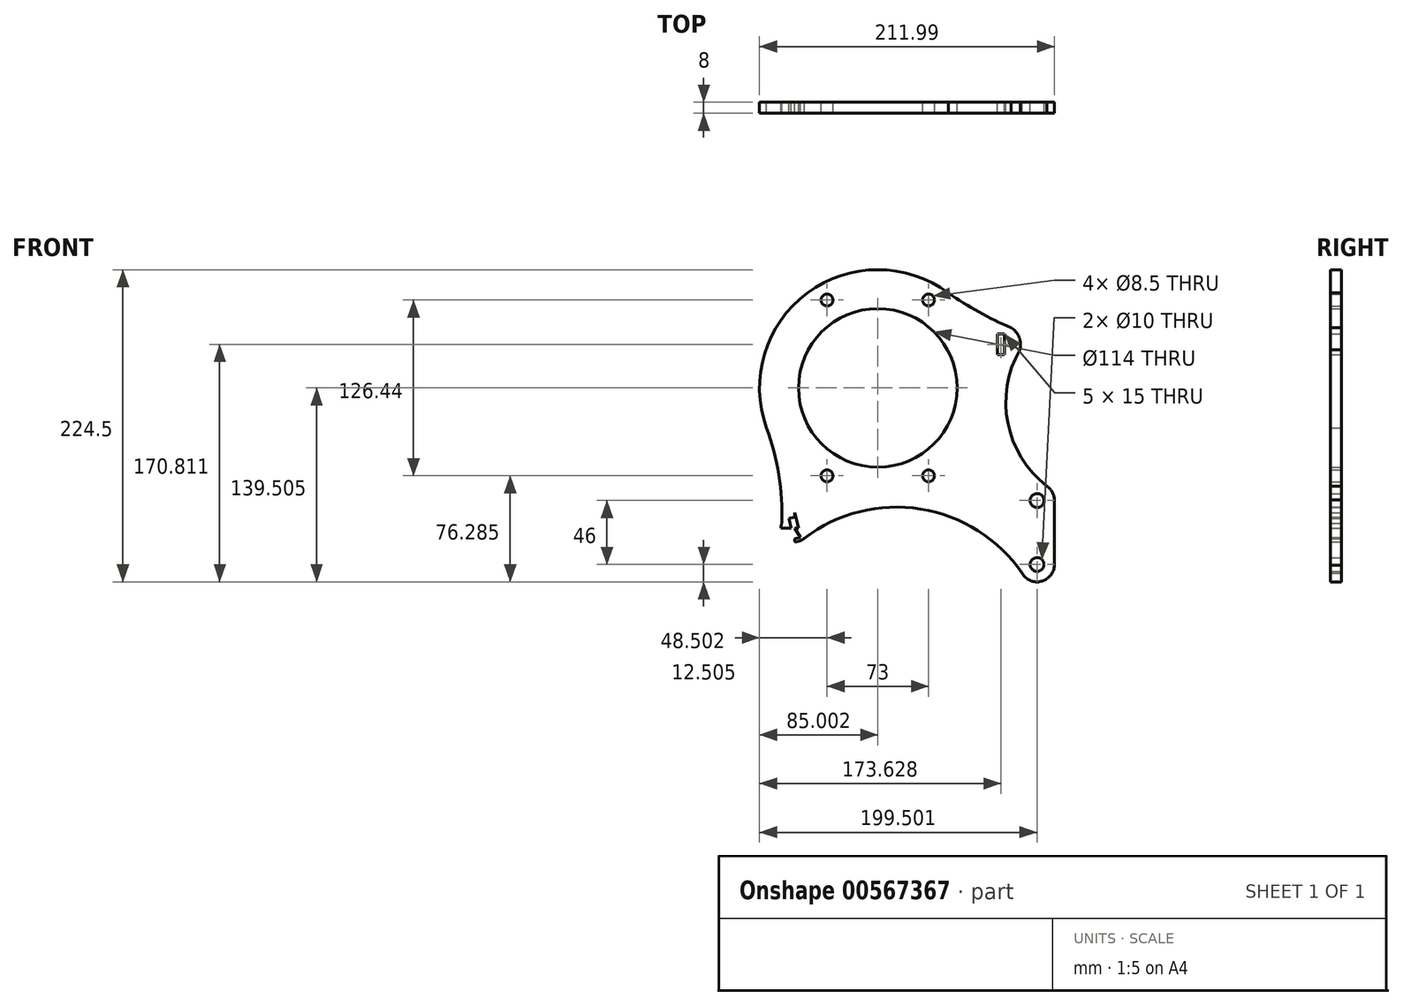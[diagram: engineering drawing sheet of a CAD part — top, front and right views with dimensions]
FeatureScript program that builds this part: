
annotation { "Feature Type Name" : "Feature", "Feature Type Description" : "" }
export const myFeature = defineFeature(function(context is Context, id is Id, definition is map)
    precondition{}
    {
        {
            var Q0;
            Q0=qCreatedBy(makeId("Front.planeOp"),FACE);
            var sketch = newSketch(context, id + "F0", { "sketchPlane" : qUnion([Q0])});
            skLineSegment(sketch, "E0", {"start": v(-75.21, -79.5) * mm, "end": v(137.4, -79.5) * mm});
            skLineSegment(sketch, "E1", {"start": v(96.05, -79.5) * mm, "end": v(96.05, -33.5) * mm});
            skCircle(sketch, "E2", {"center": v(96.05, -79.5) * mm, "radius": 5 * mm});
            skCircle(sketch, "E3", {"center": v(96.05, -33.5) * mm, "radius": 5 * mm});
            skLineSegment(sketch, "E4", {"start": v(72.68, 86.31) * mm, "end": v(72.68, 71.31) * mm});
            skLineSegment(sketch, "E5", {"start": v(72.68, 71.31) * mm, "end": v(67.68, 71.31) * mm});
            skLineSegment(sketch, "E6", {"start": v(67.68, 71.31) * mm, "end": v(67.68, 86.31) * mm});
            skLineSegment(sketch, "E7", {"start": v(22.56, -60.46) * mm, "end": v(-105.66, -60.46) * mm});
            skLineSegment(sketch, "E8", {"start": v(-45.55, -47.65) * mm, "end": v(-86.37, -47.65) * mm});
            skLineSegment(sketch, "E9", {"start": v(-80.4, -31.86) * mm, "end": v(-76.76, -47.65) * mm});
            skArc(sketch, "E10", {"start": v(85.3, -85.88) * mm, "mid": v(99.56, -91.5) * mm, "end": v(108.54, -79.1) * mm});
            skArc(sketch, "E11", {"start": v(108.54, -33.9) * mm, "mid": v(107.16, -27.77) * mm, "end": v(102.97, -23.09) * mm});
            skLineSegment(sketch, "E12", {"start": v(67.68, 86.31) * mm, "end": v(72.68, 71.31) * mm});
            skLineSegment(sketch, "E13", {"start": v(72.68, 86.31) * mm, "end": v(67.68, 71.31) * mm});
            skPoint(sketch, "E14", {"position": v(70.18, 78.81) * mm});
            skLineSegment(sketch, "E15", {"start": v(-80.4, -31.86) * mm, "end": v(-73.67, -61.07) * mm});
            skLineSegment(sketch, "E16", {"start": v(108.54, -33.1) * mm, "end": v(108.54, -79.9) * mm});
            skLineSegment(sketch, "E17", {"start": v(-77.3, -45.33) * mm, "end": v(-82.17, -46.45) * mm});
            skLineSegment(sketch, "E18", {"start": v(-82.17, -46.45) * mm, "end": v(-78.8, -61.07) * mm});
            skLineSegment(sketch, "E19", {"start": v(-78.8, -61.07) * mm, "end": v(-73.92, -59.94) * mm});
            skLineSegment(sketch, "E20", {"start": v(-77.3, -45.33) * mm, "end": v(-78.8, -61.07) * mm});
            skLineSegment(sketch, "E21", {"start": v(-82.17, -46.45) * mm, "end": v(-73.92, -59.94) * mm});
            skPoint(sketch, "E22", {"position": v(-78.05, -53.2) * mm});
            skCircle(sketch, "E23", {"center": v(-78.05, -53.2) * mm, "radius": 10 * mm});
            skLineSegment(sketch, "E24", {"start": v(-2.45, 33.5) * mm, "end": v(-113.64, 33.5) * mm});
            skLineSegment(sketch, "E25", {"start": v(-78.05, -53.2) * mm, "end": v(-78.05, -19.4) * mm});
            skLineSegment(sketch, "E26", {"start": v(-78.05, -47.35) * mm, "end": v(-78.05, -67.2) * mm});
            skLineSegment(sketch, "E27", {"start": v(-89.21, -53.2) * mm, "end": v(-73.06, -53.2) * mm});
            skLineSegment(sketch, "E28", {"start": v(-2.45, 33.5) * mm, "end": v(-2.45, -63.27) * mm});
            skLineSegment(sketch, "E29.trimOffspring", {"start": v(52.9, 86.31) * mm, "end": v(72.68, 86.31) * mm});
            skArc(sketch, "E30", {"start": v(83.65, 74.99) * mm, "mid": v(83.21, 83.92) * mm, "end": v(77.47, 90.76) * mm});
            skPoint(sketch, "E31.end.orphan", {"position": v(-78.95, 33.5) * mm});
            skArc(sketch, "E32", {"start": v(83.65, 74.99) * mm, "mid": v(75.05, 22.35) * mm, "end": v(102.97, -23.09) * mm});
            skArc(sketch, "E33", {"start": v(85.3, -85.88) * mm, "mid": v(12.4, -39.6) * mm, "end": v(-71.35, -60.62) * mm});
            skCircle(sketch, "E34", {"center": v(-18.45, 47.5) * mm, "radius": 57 * mm});
            skCircle(sketch, "E35", {"center": v(-18.45, 47.5) * mm, "radius": 73 * mm});
            skLineSegment(sketch, "E36", {"start": v(-18.45, 47.5) * mm, "end": v(-117.37, 47.5) * mm});
            skLineSegment(sketch, "E37", {"start": v(-18.45, 47.5) * mm, "end": v(-61.37, 121.85) * mm});
            skLineSegment(sketch, "E38", {"start": v(-18.45, 47.5) * mm, "end": v(25.25, 123.2) * mm});
            skLineSegment(sketch, "E39", {"start": v(-18.45, 47.5) * mm, "end": v(28.36, -33.57) * mm});
            skLineSegment(sketch, "E40", {"start": v(-18.45, 47.5) * mm, "end": v(-53.64, -13.44) * mm});
            skCircle(sketch, "E41", {"center": v(-54.95, 110.72) * mm, "radius": 4.25 * mm});
            skCircle(sketch, "E42", {"center": v(18.05, 110.72) * mm, "radius": 4.25 * mm});
            skCircle(sketch, "E43", {"center": v(18.05, -15.72) * mm, "radius": 4.25 * mm});
            skCircle(sketch, "E44", {"center": v(-54.95, -15.72) * mm, "radius": 4.25 * mm});
            skCircle(sketch, "E45", {"center": v(-18.45, 47.5) * mm, "radius": 85 * mm});
            skArc(sketch, "E46", {"start": v(-87.5, -49.93) * mm, "mid": v(-89.52, -15.05) * mm, "end": v(-98.43, 18.74) * mm});
            skArc(sketch, "E47", {"start": v(32.24, 115.74) * mm, "mid": v(54.23, 102.13) * mm, "end": v(77.47, 90.76) * mm});
            skSolve(sketch);
        }
        {
            var Q0;
            {var subQ1=sQuery(id+"F0.wireOp",EDGE,"E8");var subQ5=sQuery(id+"F0.wireOp",EDGE,"E33");var subQ6=makeQuery(id+"F0.imprint","INTERSECT",VERTEX,{"derivedFrom":[subQ1,subQ5]});Q0=makeQuery(id+"F0.imprint","IMPRINT",FACE,{"disambiguationData":[TD([[makeQuery(id+"F0.imprint","IMPRINT",EDGE,{"disambiguationData":[TD([[subQ6,-1.0]])],"derivedFrom":subQ1}),-1.0]])]});}
            var Q1;
            {var subQ0=sQuery(id+"F0.wireOp",EDGE,"E23");var subQ1=sQuery(id+"F0.wireOp",EDGE,"E8");var subQ2=makeQuery(id+"F0.imprint","INTERSECT",VERTEX,{"disambiguationData":[OD(0.0)],"derivedFrom":[subQ1,subQ0]});Q1=makeQuery(id+"F0.imprint","IMPRINT",FACE,{"disambiguationData":[TD([[makeQuery(id+"F0.imprint","IMPRINT",EDGE,{"disambiguationData":[TD([[subQ2,1.0]])],"derivedFrom":subQ1}),1.0]])]});}
            var Q2;
            {var subQ0=sQuery(id+"F0.wireOp",EDGE,"E23");var subQ1=sQuery(id+"F0.wireOp",EDGE,"E8");var subQ2=makeQuery(id+"F0.imprint","INTERSECT",VERTEX,{"disambiguationData":[OD(0.0)],"derivedFrom":[subQ1,subQ0]});Q2=makeQuery(id+"F0.imprint","IMPRINT",FACE,{"disambiguationData":[TD([[makeQuery(id+"F0.imprint","IMPRINT",EDGE,{"disambiguationData":[TD([[subQ2,1.0]])],"derivedFrom":subQ1}),-1.0]])]});}
            var Q3;
            {var subQ0=sQuery(id+"F0.wireOp",EDGE,"E23");var subQ1=sQuery(id+"F0.wireOp",EDGE,"E8");var subQ2=makeQuery(id+"F0.imprint","INTERSECT",VERTEX,{"disambiguationData":[OD(1.0)],"derivedFrom":[subQ1,subQ0]});Q3=makeQuery(id+"F0.imprint","IMPRINT",FACE,{"disambiguationData":[TD([[makeQuery(id+"F0.imprint","IMPRINT",EDGE,{"disambiguationData":[TD([[subQ2,-1.0]])],"derivedFrom":subQ1}),-1.0]])]});}
            var Q4;
            {var subQ0=sQuery(id+"F0.wireOp",EDGE,"E15");var subQ7=sQuery(id+"F0.wireOp",EDGE,"E7");var subQ8=makeQuery(id+"F0.imprint","INTERSECT",VERTEX,{"derivedFrom":[subQ7,subQ0]});Q4=makeQuery(id+"F0.imprint","IMPRINT",FACE,{"disambiguationData":[TD([[makeQuery(id+"F0.imprint","IMPRINT",EDGE,{"disambiguationData":[TD([[subQ8,1.0]])],"derivedFrom":subQ7}),-1.0]])]});}
            var Q5;
            {var subQ1=sQuery(id+"F0.wireOp",EDGE,"E7");var subQ5=makeQuery(id+"F0.imprint","INTERSECT",VERTEX,{"derivedFrom":[subQ1,sQuery(id+"F0.wireOp",EDGE,"E15")]});Q5=makeQuery(id+"F0.imprint","IMPRINT",FACE,{"disambiguationData":[TD([[makeQuery(id+"F0.imprint","IMPRINT",EDGE,{"disambiguationData":[TD([[subQ5,1.0]])],"derivedFrom":subQ1}),1.0]])]});}
            var Q6;
            {var subQ0=sQuery(id+"F0.wireOp",EDGE,"E23");var subQ1=sQuery(id+"F0.wireOp",EDGE,"E7");var subQ2=makeQuery(id+"F0.imprint","INTERSECT",VERTEX,{"disambiguationData":[OD(0.0)],"derivedFrom":[subQ1,subQ0]});Q6=makeQuery(id+"F0.imprint","IMPRINT",FACE,{"disambiguationData":[TD([[makeQuery(id+"F0.imprint","IMPRINT",EDGE,{"disambiguationData":[TD([[subQ2,1.0]])],"derivedFrom":subQ1}),-1.0]])]});}
            var Q7;
            {var subQ0=sQuery(id+"F0.wireOp",EDGE,"E23");var subQ1=sQuery(id+"F0.wireOp",EDGE,"E7");var subQ2=makeQuery(id+"F0.imprint","INTERSECT",VERTEX,{"disambiguationData":[OD(0.0)],"derivedFrom":[subQ1,subQ0]});Q7=makeQuery(id+"F0.imprint","IMPRINT",FACE,{"disambiguationData":[TD([[makeQuery(id+"F0.imprint","IMPRINT",EDGE,{"disambiguationData":[TD([[subQ2,1.0]])],"derivedFrom":subQ1}),1.0]])]});}
            var Q8;
            {var subQ0=sQuery(id+"F0.wireOp",EDGE,"E15");var subQ1=sQuery(id+"F0.wireOp",EDGE,"E7");var subQ2=makeQuery(id+"F0.imprint","INTERSECT",VERTEX,{"derivedFrom":[subQ1,subQ0]});Q8=makeQuery(id+"F0.imprint","IMPRINT",FACE,{"disambiguationData":[TD([[makeQuery(id+"F0.imprint","IMPRINT",EDGE,{"disambiguationData":[TD([[subQ2,-1.0]])],"derivedFrom":subQ1}),-1.0]])]});}
            var Q9;
            {var subQ0=sQuery(id+"F0.wireOp",EDGE,"E33");var subQ1=sQuery(id+"F0.wireOp",EDGE,"E7");var subQ2=makeQuery(id+"F0.imprint","INTERSECT",VERTEX,{"derivedFrom":[subQ1,subQ0]});Q9=makeQuery(id+"F0.imprint","IMPRINT",FACE,{"disambiguationData":[TD([[makeQuery(id+"F0.imprint","IMPRINT",EDGE,{"disambiguationData":[TD([[subQ2,-1.0]])],"derivedFrom":subQ1}),-1.0]])]});}
            var Q10;
            {var subQ1=sQuery(id+"F0.wireOp",EDGE,"E15");var subQ3=sQuery(id+"F0.wireOp",EDGE,"E23");var subQ4=makeQuery(id+"F0.imprint","INTERSECT",VERTEX,{"derivedFrom":[subQ1,subQ3]});Q10=makeQuery(id+"F0.imprint","IMPRINT",FACE,{"disambiguationData":[TD([[makeQuery(id+"F0.imprint","IMPRINT",EDGE,{"disambiguationData":[TD([[subQ4,-1.0]])],"derivedFrom":subQ3}),1.0]])]});}
            var Q11;
            {var subQ0=sQuery(id+"F0.wireOp",EDGE,"E25");var subQ1=sQuery(id+"F0.wireOp",EDGE,"E15");var subQ2=makeQuery(id+"F0.imprint","INTERSECT",VERTEX,{"derivedFrom":[subQ1,subQ0]});Q11=makeQuery(id+"F0.imprint","IMPRINT",FACE,{"disambiguationData":[TD([[makeQuery(id+"F0.imprint","IMPRINT",EDGE,{"disambiguationData":[TD([[subQ2,-1.0]])],"derivedFrom":subQ1}),-1.0]])]});}
            var Q12;
            {var subQ5=sQuery(id+"F0.wireOp",EDGE,"E24");var subQ8=sQuery(id+"F0.wireOp",EDGE,"E45");var subQ12=makeQuery(id+"F0.imprint","INTERSECT",VERTEX,{"derivedFrom":[subQ5,subQ8]});Q12=makeQuery(id+"F0.imprint","IMPRINT",FACE,{"disambiguationData":[TD([[makeQuery(id+"F0.imprint","IMPRINT",EDGE,{"disambiguationData":[TD([[subQ12,1.0]])],"derivedFrom":subQ5}),1.0]])]});}
            var Q13;
            {var subQ1=sQuery(id+"F0.wireOp",EDGE,"E28");var subQ5=sQuery(id+"F0.wireOp",EDGE,"E34");var subQ6=makeQuery(id+"F0.imprint","INTERSECT",VERTEX,{"derivedFrom":[subQ1,subQ5]});Q13=makeQuery(id+"F0.imprint","IMPRINT",FACE,{"disambiguationData":[TD([[makeQuery(id+"F0.imprint","IMPRINT",EDGE,{"disambiguationData":[TD([[subQ6,-1.0]])],"derivedFrom":subQ1}),-1.0]])]});}
            var Q14;
            {var subQ1=sQuery(id+"F0.wireOp",EDGE,"E24");var subQ5=sQuery(id+"F0.wireOp",EDGE,"E34");var subQ6=makeQuery(id+"F0.imprint","INTERSECT",VERTEX,{"derivedFrom":[subQ1,subQ5]});Q14=makeQuery(id+"F0.imprint","IMPRINT",FACE,{"disambiguationData":[TD([[makeQuery(id+"F0.imprint","IMPRINT",EDGE,{"disambiguationData":[TD([[subQ6,-1.0]])],"derivedFrom":subQ1}),1.0]])]});}
            var Q15;
            {var subQ1=sQuery(id+"F0.wireOp",EDGE,"E34");var subQ6=sQuery(id+"F0.wireOp",EDGE,"E28");var subQ9=makeQuery(id+"F0.imprint","INTERSECT",VERTEX,{"derivedFrom":[subQ6,subQ1]});Q15=makeQuery(id+"F0.imprint","IMPRINT",FACE,{"disambiguationData":[TD([[makeQuery(id+"F0.imprint","IMPRINT",EDGE,{"disambiguationData":[TD([[subQ9,-1.0]])],"derivedFrom":subQ6}),1.0]])]});}
            var Q16;
            {var subQ5=sQuery(id+"F0.wireOp",EDGE,"E35");var subQ6=sQuery(id+"F0.wireOp",EDGE,"E28");var subQ7=makeQuery(id+"F0.imprint","INTERSECT",VERTEX,{"derivedFrom":[subQ6,subQ5]});Q16=makeQuery(id+"F0.imprint","IMPRINT",FACE,{"disambiguationData":[TD([[makeQuery(id+"F0.imprint","IMPRINT",EDGE,{"disambiguationData":[TD([[subQ7,-1.0]])],"derivedFrom":subQ6}),1.0]])]});}
            var Q17;
            Q17=makeQuery(id+"F0.imprint","IMPRINT",FACE,{"disambiguationData":[TD([[makeQuery(id+"F0.imprint","IMPRINT",EDGE,{"derivedFrom":sQuery(id+"F0.wireOp",EDGE,"E3")}),-1.0]])]});
            var Q18;
            {var subQ5=sQuery(id+"F0.wireOp",EDGE,"E45");var subQ13=makeQuery(id+"F0.imprint","IMPRINT",VERTEX,{"derivedFrom":subQ5});Q18=makeQuery(id+"F0.imprint","IMPRINT",FACE,{"disambiguationData":[TD([[makeQuery(id+"F0.imprint","IMPRINT",EDGE,{"disambiguationData":[TD([[subQ13,-1.0]])],"derivedFrom":subQ5}),1.0]])]});}
            var Q19;
            {var subQ1=sQuery(id+"F0.wireOp",EDGE,"E34");var subQ5=sQuery(id+"F0.wireOp",EDGE,"E38");var subQ6=makeQuery(id+"F0.imprint","INTERSECT",VERTEX,{"derivedFrom":[subQ1,subQ5]});Q19=makeQuery(id+"F0.imprint","IMPRINT",FACE,{"disambiguationData":[TD([[makeQuery(id+"F0.imprint","IMPRINT",EDGE,{"disambiguationData":[TD([[subQ6,1.0]])],"derivedFrom":subQ1}),-1.0]])]});}
            var Q20;
            {var subQ0=sQuery(id+"F0.wireOp",EDGE,"E33");var subQ6=sQuery(id+"F0.wireOp",EDGE,"E0");var subQ10=makeQuery(id+"F0.imprint","INTERSECT",VERTEX,{"derivedFrom":[subQ6,subQ0]});Q20=makeQuery(id+"F0.imprint","IMPRINT",FACE,{"disambiguationData":[TD([[makeQuery(id+"F0.imprint","IMPRINT",EDGE,{"disambiguationData":[TD([[subQ10,-1.0]])],"derivedFrom":subQ6}),-1.0]])]});}
            var Q21;
            {var subQ6=sQuery(id+"F0.wireOp",EDGE,"E34");var subQ9=sQuery(id+"F0.wireOp",EDGE,"E37");var subQ10=makeQuery(id+"F0.imprint","INTERSECT",VERTEX,{"derivedFrom":[subQ6,subQ9]});Q21=makeQuery(id+"F0.imprint","IMPRINT",FACE,{"disambiguationData":[TD([[makeQuery(id+"F0.imprint","IMPRINT",EDGE,{"disambiguationData":[TD([[subQ10,1.0]])],"derivedFrom":subQ6}),-1.0]])]});}
            var Q22;
            {var subQ3=sQuery(id+"F0.wireOp",EDGE,"E42");var subQ6=sQuery(id+"F0.wireOp",EDGE,"E35");var subQ11=makeQuery(id+"F0.imprint","INTERSECT",VERTEX,{"disambiguationData":[OD(1.0)],"derivedFrom":[subQ6,subQ3]});Q22=makeQuery(id+"F0.imprint","IMPRINT",FACE,{"disambiguationData":[TD([[makeQuery(id+"F0.imprint","IMPRINT",EDGE,{"disambiguationData":[TD([[subQ11,-1.0]])],"derivedFrom":subQ6}),-1.0]])]});}
            var Q23;
            {var subQ0=sQuery(id+"F0.wireOp",EDGE,"E37");var subQ1=sQuery(id+"F0.wireOp",EDGE,"E34");var subQ2=makeQuery(id+"F0.imprint","INTERSECT",VERTEX,{"derivedFrom":[subQ1,subQ0]});Q23=makeQuery(id+"F0.imprint","IMPRINT",FACE,{"disambiguationData":[TD([[makeQuery(id+"F0.imprint","IMPRINT",EDGE,{"disambiguationData":[TD([[subQ2,-1.0]])],"derivedFrom":subQ1}),-1.0]])]});}
            var Q24;
            {var subQ0=sQuery(id+"F0.wireOp",EDGE,"E41");var subQ1=sQuery(id+"F0.wireOp",EDGE,"E35");var subQ2=makeQuery(id+"F0.imprint","INTERSECT",VERTEX,{"disambiguationData":[OD(1.0)],"derivedFrom":[subQ1,subQ0]});Q24=makeQuery(id+"F0.imprint","IMPRINT",FACE,{"disambiguationData":[TD([[makeQuery(id+"F0.imprint","IMPRINT",EDGE,{"disambiguationData":[TD([[subQ2,-1.0]])],"derivedFrom":subQ1}),-1.0]])]});}
            var Q25;
            {var subQ0=sQuery(id+"F0.wireOp",EDGE,"E45");var subQ1=sQuery(id+"F0.wireOp",EDGE,"E24");var subQ2=makeQuery(id+"F0.imprint","INTERSECT",VERTEX,{"derivedFrom":[subQ1,subQ0]});Q25=makeQuery(id+"F0.imprint","IMPRINT",FACE,{"disambiguationData":[TD([[makeQuery(id+"F0.imprint","IMPRINT",EDGE,{"disambiguationData":[TD([[subQ2,1.0]])],"derivedFrom":subQ1}),-1.0]])]});}
            var Q26;
            {var subQ0=sQuery(id+"F0.wireOp",EDGE,"E34");var subQ1=sQuery(id+"F0.wireOp",EDGE,"E24");var subQ2=makeQuery(id+"F0.imprint","INTERSECT",VERTEX,{"derivedFrom":[subQ1,subQ0]});Q26=makeQuery(id+"F0.imprint","IMPRINT",FACE,{"disambiguationData":[TD([[makeQuery(id+"F0.imprint","IMPRINT",EDGE,{"disambiguationData":[TD([[subQ2,-1.0]])],"derivedFrom":subQ1}),-1.0]])]});}
            extrude(context, id + "F1", {"entities" : qUnion([Q0, Q1, Q2, Q3, Q4, Q5, Q6, Q7, Q8, Q9, Q10, Q11, Q12, Q13, Q14, Q15, Q16, Q17, Q18, Q19, Q20, Q21, Q22, Q23, Q24, Q25, Q26]), "depth" : 8 * mm, "offsetDistance" : 25 * mm});
        }
    });
